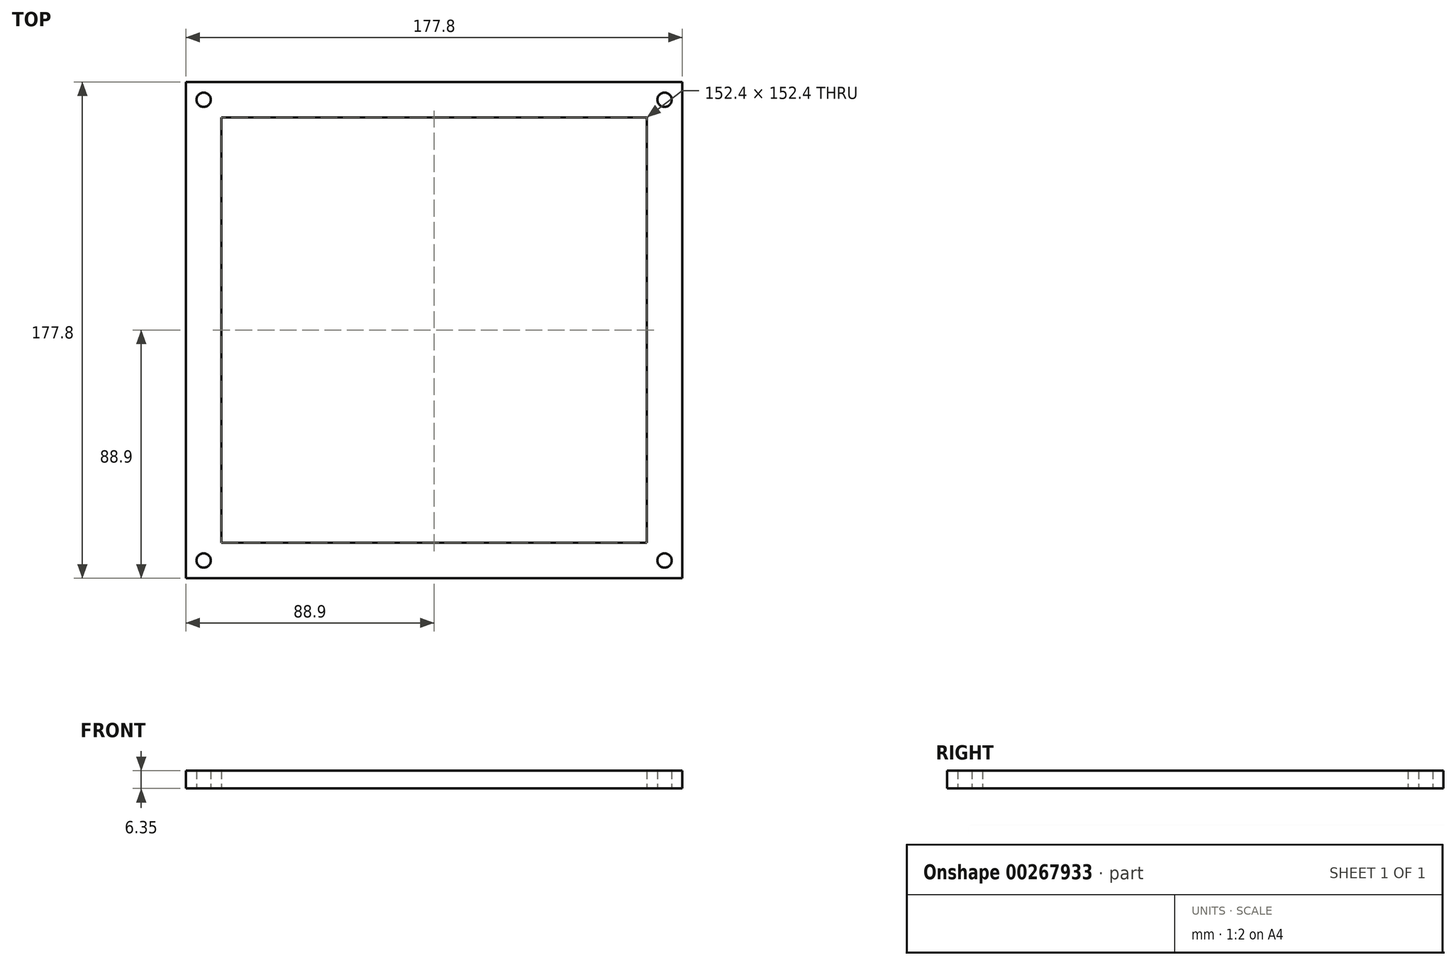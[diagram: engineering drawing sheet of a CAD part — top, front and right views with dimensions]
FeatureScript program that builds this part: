
annotation { "Feature Type Name" : "Feature", "Feature Type Description" : "" }
export const myFeature = defineFeature(function(context is Context, id is Id, definition is map)
    precondition{}
    {
        {
            var Q0;
            Q0=qCreatedBy(makeId("Top.planeOp"),FACE);
            var sketch = newSketch(context, id + "F0", { "sketchPlane" : qUnion([Q0])});
            skLineSegment(sketch, "E0.bottom", {"start": v(-76.2, 76.2) * mm, "end": v(76.2, 76.2) * mm});
            skLineSegment(sketch, "E0.top", {"start": v(-76.2, -76.2) * mm, "end": v(76.2, -76.2) * mm});
            skLineSegment(sketch, "E0.left", {"start": v(-76.2, 76.2) * mm, "end": v(-76.2, -76.2) * mm});
            skLineSegment(sketch, "E0.right", {"start": v(76.2, 76.2) * mm, "end": v(76.2, -76.2) * mm});
            skPoint(sketch, "E0.middle", {"position": v(0, 0) * mm});
            skLineSegment(sketch, "E1.bottom", {"start": v(-88.9, 88.9) * mm, "end": v(88.9, 88.9) * mm});
            skLineSegment(sketch, "E1.top", {"start": v(-88.9, -88.9) * mm, "end": v(88.9, -88.9) * mm});
            skLineSegment(sketch, "E1.left", {"start": v(-88.9, 88.9) * mm, "end": v(-88.9, -88.9) * mm});
            skLineSegment(sketch, "E1.right", {"start": v(88.9, 88.9) * mm, "end": v(88.9, -88.9) * mm});
            skLineSegment(sketch, "E2.bottom", {"start": v(-82.55, 82.55) * mm, "end": v(82.55, 82.55) * mm, "construction": true});
            skLineSegment(sketch, "E2.top", {"start": v(-82.55, -82.55) * mm, "end": v(82.55, -82.55) * mm, "construction": true});
            skLineSegment(sketch, "E2.left", {"start": v(-82.55, 82.55) * mm, "end": v(-82.55, -82.55) * mm, "construction": true});
            skLineSegment(sketch, "E2.right", {"start": v(82.55, 82.55) * mm, "end": v(82.55, -82.55) * mm, "construction": true});
            skCircle(sketch, "E3", {"center": v(-82.55, 82.55) * mm, "radius": 2.55 * mm});
            skCircle(sketch, "E4", {"center": v(82.55, 82.55) * mm, "radius": 2.55 * mm});
            skCircle(sketch, "E5", {"center": v(-82.55, -82.55) * mm, "radius": 2.55 * mm});
            skCircle(sketch, "E6", {"center": v(82.55, -82.55) * mm, "radius": 2.55 * mm});
            skSolve(sketch);
        }
        {
            var Q0;
            Q0=makeQuery(id+"F0.imprint","IMPRINT",FACE,{"disambiguationData":[TD([[makeQuery(id+"F0.imprint","IMPRINT",EDGE,{"derivedFrom":sQuery(id+"F0.wireOp",EDGE,"E0.bottom")}),1.0]])]});
            extrude(context, id + "F1", {"entities" : qUnion([Q0]), "depth" : 6.35 * mm, "offsetDistance" : 25.4 * mm});
        }
    });
